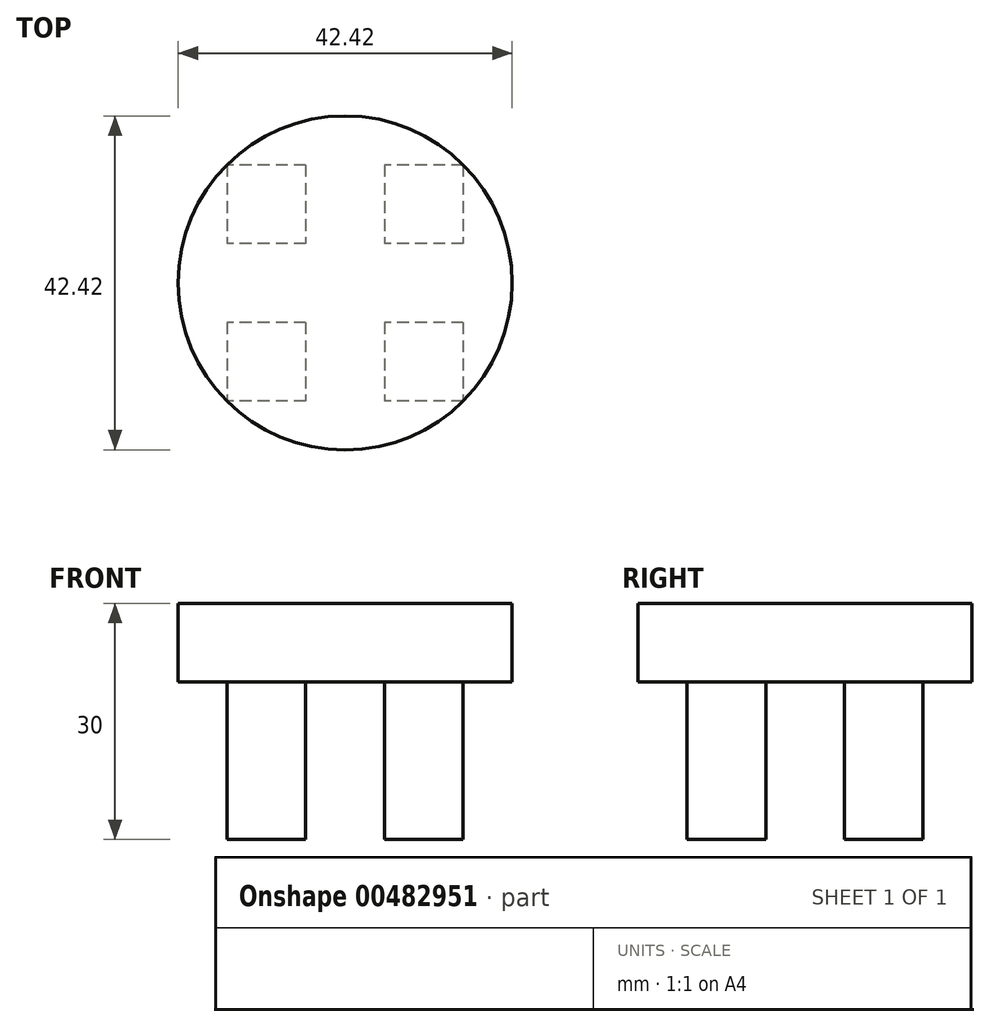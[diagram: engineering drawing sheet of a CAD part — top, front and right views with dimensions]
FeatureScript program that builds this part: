
annotation { "Feature Type Name" : "Feature", "Feature Type Description" : "" }
export const myFeature = defineFeature(function(context is Context, id is Id, definition is map)
    precondition{}
    {
        {
            var Q0;
            Q0=qCreatedBy(makeId("Top.planeOp"),FACE);
            var sketch = newSketch(context, id + "F0", { "sketchPlane" : qUnion([Q0])});
            skLineSegment(sketch, "E0.bottom", {"start": v(15, 15) * mm, "end": v(-15, 15) * mm});
            skLineSegment(sketch, "E0.top", {"start": v(15, -15) * mm, "end": v(-15, -15) * mm});
            skLineSegment(sketch, "E0.left", {"start": v(15, 15) * mm, "end": v(15, -15) * mm});
            skLineSegment(sketch, "E0.right", {"start": v(-15, 15) * mm, "end": v(-15, -15) * mm});
            skPoint(sketch, "E0.middle", {"position": v(0, 0) * mm});
            skSolve(sketch);
        }
        {
            var Q0;
            Q0=makeQuery(id+"F0.imprint","IMPRINT",FACE,{"disambiguationData":[TD([[makeQuery(id+"F0.imprint","IMPRINT",EDGE,{"derivedFrom":sQuery(id+"F0.wireOp",EDGE,"E0.bottom")}),1.0]])]});
            extrude(context, id + "F1", {"entities" : qUnion([Q0]), "depth" : 30 * mm});
        }
        {
            var Q0;
            Q0=makeQuery(id+"F1.opExtrude","SWEPT_FACE",FACE,{"disambiguationData":[OSD([sQuery(id+"F0.wireOp",EDGE,"E0.top")])]});
            var sketch = newSketch(context, id + "F2", { "sketchPlane" : qUnion([Q0])});
            skLineSegment(sketch, "E1", {"start": v(-15, 0) * mm, "end": v(-5, 0) * mm});
            skLineSegment(sketch, "E2", {"start": v(15, 0) * mm, "end": v(5, 0) * mm});
            skLineSegment(sketch, "E3.bottom", {"start": v(-5, 0) * mm, "end": v(5, 0) * mm});
            skLineSegment(sketch, "E3.top", {"start": v(-5, 20) * mm, "end": v(5, 20) * mm});
            skLineSegment(sketch, "E3.left", {"start": v(-5, 0) * mm, "end": v(-5, 20) * mm});
            skLineSegment(sketch, "E3.right", {"start": v(5, 0) * mm, "end": v(5, 20) * mm});
            skSolve(sketch);
        }
        {
            var Q0;
            Q0=makeQuery(id+"F2.imprint","IMPRINT",FACE,{"disambiguationData":[TD([[makeQuery(id+"F2.imprint","IMPRINT",EDGE,{"derivedFrom":sQuery(id+"F2.wireOp",EDGE,"E3.bottom")}),-1.0]])]});
            extrude(context, id + "F3", {"entities" : qUnion([Q0]), "operationType" : NewBodyOperationType.REMOVE, "oppositeDirection" : true, "depth" : 30 * mm});
        }
        {
            var Q0;
            Q0=makeQuery(id+"F1.opExtrude","SWEPT_FACE",FACE,{"disambiguationData":[OSD([sQuery(id+"F0.wireOp",EDGE,"E0.right")])]});
            var sketch = newSketch(context, id + "F4", { "sketchPlane" : qUnion([Q0])});
            skLineSegment(sketch, "E4", {"start": v(-15, 0) * mm, "end": v(-5, 0) * mm});
            skLineSegment(sketch, "E5", {"start": v(15, 0) * mm, "end": v(5, 0) * mm});
            skLineSegment(sketch, "E6.bottom", {"start": v(-5, 0) * mm, "end": v(5, 0) * mm});
            skLineSegment(sketch, "E6.top", {"start": v(-5, 20) * mm, "end": v(5, 20) * mm});
            skLineSegment(sketch, "E6.left", {"start": v(-5, 0) * mm, "end": v(-5, 20) * mm});
            skLineSegment(sketch, "E6.right", {"start": v(5, 0) * mm, "end": v(5, 20) * mm});
            skSolve(sketch);
        }
        {
            var Q0;
            Q0=makeQuery(id+"F4.imprint","IMPRINT",FACE,{"disambiguationData":[TD([[makeQuery(id+"F4.imprint","IMPRINT",EDGE,{"derivedFrom":sQuery(id+"F4.wireOp",EDGE,"E6.bottom")}),1.0]])]});
            extrude(context, id + "F5", {"entities" : qUnion([Q0]), "operationType" : NewBodyOperationType.REMOVE, "oppositeDirection" : true, "depth" : 30 * mm});
        }
        {
            var Q0;
            Q0=makeQuery(id+"F1.opExtrude","CAP_FACE",FACE,{"disambiguationData":[OSD([sQuery(id+"F0.wireOp",EDGE,"E0.bottom"),sQuery(id+"F0.wireOp",EDGE,"E0.top"),sQuery(id+"F0.wireOp",EDGE,"E0.left"),sQuery(id+"F0.wireOp",EDGE,"E0.right")])],"isStart":false});
            var sketch = newSketch(context, id + "F6", { "sketchPlane" : qUnion([Q0])});
            skCircle(sketch, "E7", {"center": v(0, 0) * mm, "radius": 21.21 * mm});
            skSolve(sketch);
        }
        {
            var Q0;
            Q0 = qSketchRegion(id + "F6", true);
            extrude(context, id + "F7", {"entities" : qUnion([Q0]), "operationType" : NewBodyOperationType.ADD, "oppositeDirection" : true, "depth" : 10 * mm});
        }
    });
